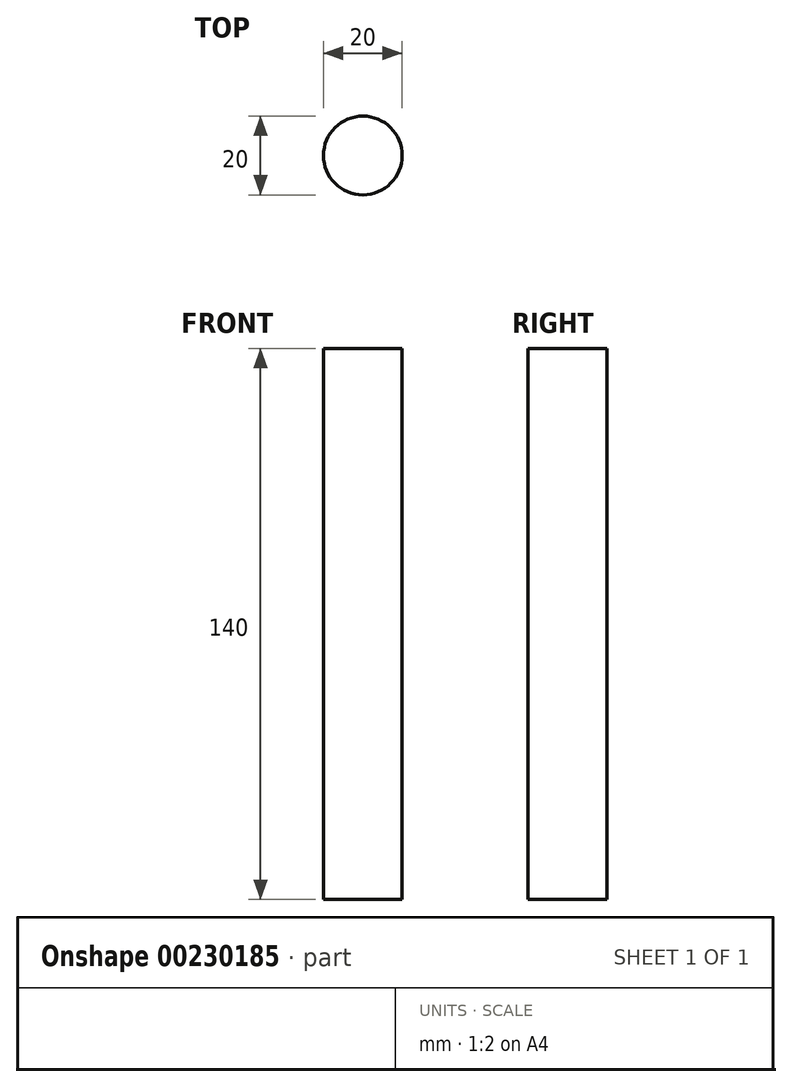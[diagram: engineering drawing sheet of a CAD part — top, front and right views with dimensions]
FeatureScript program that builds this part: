
annotation { "Feature Type Name" : "Feature", "Feature Type Description" : "" }
export const myFeature = defineFeature(function(context is Context, id is Id, definition is map)
    precondition{}
    {
        {
            var Q0;
            Q0=qCreatedBy(makeId("Top.planeOp"),FACE);
            var sketch = newSketch(context, id + "F0", { "sketchPlane" : qUnion([Q0])});
            skCircle(sketch, "E0", {"center": v(0, 0) * mm, "radius": 10 * mm});
            skSolve(sketch);
        }
        {
            var Q0;
            Q0 = qSketchRegion(id + "F0", true);
            extrude(context, id + "F1", {"entities" : qUnion([Q0]), "depth" : 140 * mm});
        }
    });
